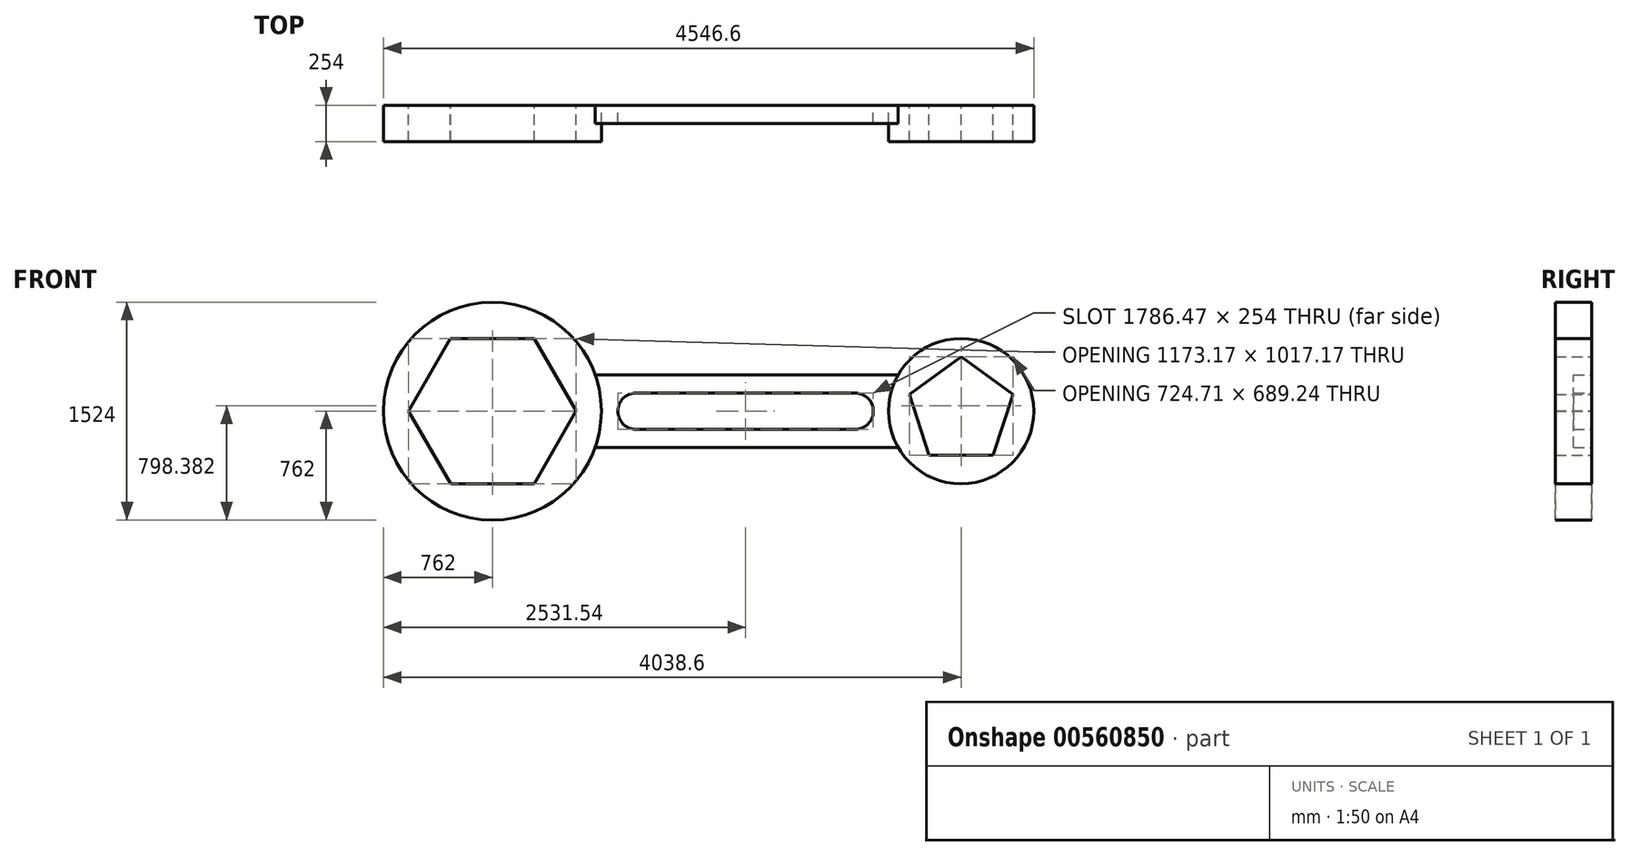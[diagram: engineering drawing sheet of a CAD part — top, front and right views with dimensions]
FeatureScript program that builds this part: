
annotation { "Feature Type Name" : "Feature", "Feature Type Description" : "" }
export const myFeature = defineFeature(function(context is Context, id is Id, definition is map)
    precondition{}
    {
        {
            var Q0;
            Q0=qCreatedBy(makeId("Front.planeOp"),FACE);
            var sketch = newSketch(context, id + "F0", { "sketchPlane" : qUnion([Q0])});
            skCircle(sketch, "E0", {"center": v(0, 0) * mm, "radius": 762 * mm});
            skLineSegment(sketch, "E1", {"start": v(762, 0) * mm, "end": v(2768.6, 0) * mm});
            skCircle(sketch, "E2", {"center": v(3276.6, 0) * mm, "radius": 508 * mm});
            skLineSegment(sketch, "E3", {"start": v(1765.3, 0) * mm, "end": v(1765.3, 127) * mm});
            skLineSegment(sketch, "E4", {"start": v(1765.3, 127) * mm, "end": v(1003.3, 127) * mm});
            skLineSegment(sketch, "E5", {"start": v(1003.3, -127) * mm, "end": v(2535.77, -127) * mm});
            skLineSegment(sketch, "E6", {"start": v(2535.77, 127) * mm, "end": v(1765.3, 127) * mm});
            skLineSegment(sketch, "E7", {"start": v(1765.3, 0) * mm, "end": v(1765.3, 254) * mm});
            skPoint(sketch, "E7.endSnap0", {"position": v(1765.3, 63.5) * mm});
            skLineSegment(sketch, "E8", {"start": v(1765.3, 254) * mm, "end": v(718.42, 254) * mm});
            skLineSegment(sketch, "E9", {"start": v(1765.3, 254) * mm, "end": v(2836.66, 254) * mm});
            skLineSegment(sketch, "E10.MirrorCS", {"start": v(750.33, 0) * mm, "end": v(2756.93, 0) * mm});
            skLineSegment(sketch, "E11.MirrorCS", {"start": v(1765.3, -254) * mm, "end": v(2836.66, -254) * mm});
            skLineSegment(sketch, "E12.MirrorCS", {"start": v(1765.3, -254) * mm, "end": v(718.42, -254) * mm});
            skCircle(sketch, "E13.cCircle", {"center": v(0, 0) * mm, "radius": 508 * mm, "construction": true});
            skLineSegment(sketch, "E13.0", {"start": v(292.28, 508.58) * mm, "end": v(586.59, 1.17) * mm});
            skLineSegment(sketch, "E13.1", {"start": v(586.59, 1.17) * mm, "end": v(294.3, -507.41) * mm});
            skLineSegment(sketch, "E13.2", {"start": v(294.3, -507.41) * mm, "end": v(-292.28, -508.58) * mm});
            skLineSegment(sketch, "E13.3", {"start": v(-292.28, -508.58) * mm, "end": v(-586.59, -1.17) * mm});
            skLineSegment(sketch, "E13.4", {"start": v(-586.59, -1.17) * mm, "end": v(-294.3, 507.41) * mm});
            skLineSegment(sketch, "E13.5", {"start": v(-294.3, 507.41) * mm, "end": v(292.28, 508.58) * mm});
            skPoint(sketch, "E13.0.midPoint", {"position": v(439.43, 254.88) * mm});
            skCircle(sketch, "E14.cCircle", {"center": v(3276.6, 0) * mm, "radius": 308.24 * mm, "construction": true});
            skLineSegment(sketch, "E14.0", {"start": v(2914.25, 117.73) * mm, "end": v(3276.6, 381) * mm});
            skLineSegment(sketch, "E14.1", {"start": v(3276.6, 381) * mm, "end": v(3638.95, 117.74) * mm});
            skLineSegment(sketch, "E14.2", {"start": v(3638.95, 117.74) * mm, "end": v(3500.55, -308.23) * mm});
            skLineSegment(sketch, "E14.3", {"start": v(3500.55, -308.23) * mm, "end": v(3052.66, -308.24) * mm});
            skLineSegment(sketch, "E14.4", {"start": v(3052.66, -308.24) * mm, "end": v(2914.25, 117.73) * mm});
            skPoint(sketch, "E14.0.midPoint", {"position": v(3095.42, 249.37) * mm});
            skLineSegment(sketch, "E15", {"start": v(3276.6, 381) * mm, "end": v(3276.6, 0) * mm});
            skLineSegment(sketch, "E16", {"start": v(0, 508) * mm, "end": v(0, 0) * mm});
            skPoint(sketch, "E17.visualSharp", {"position": v(876.3, 127) * mm});
            skArc(sketch, "E18", {"start": v(1003.3, 127) * mm, "mid": v(876.3, 0) * mm, "end": v(1003.3, -127) * mm});
            skPoint(sketch, "E19.orphan", {"position": v(876.3, -127) * mm});
            skArc(sketch, "E20", {"start": v(2535.77, -127) * mm, "mid": v(2662.77, 0) * mm, "end": v(2535.77, 127) * mm});
            skSolve(sketch);
        }
        {
            var Q0;
            {var subQ5=sQuery(id+"F0.wireOp",EDGE,"E13.0");Q0=makeQuery(id+"F0.imprint","IMPRINT",FACE,{"disambiguationData":[TD([[makeQuery(id+"F0.imprint","IMPRINT",EDGE,{"derivedFrom":subQ5}),1.0]])]});}
            var Q1;
            Q1=makeQuery(id+"F0.imprint","IMPRINT",FACE,{"disambiguationData":[TD([[makeQuery(id+"F0.imprint","IMPRINT",EDGE,{"derivedFrom":sQuery(id+"F0.wireOp",EDGE,"E14.0")}),1.0]])]});
            extrude(context, id + "F1", {"entities" : qUnion([Q0, Q1]), "depth" : 254 * mm, "offsetDistance" : 25.4 * mm});
        }
        {
            var Q0;
            {var subQ4=sQuery(id+"F0.wireOp",EDGE,"E1");Q0=makeQuery(id+"F0.imprint","IMPRINT",FACE,{"disambiguationData":[TD([[makeQuery(id+"F0.imprint","IMPRINT",EDGE,{"derivedFrom":subQ4}),1.0]])]});}
            var Q1;
            {var subQ1=sQuery(id+"F0.wireOp",EDGE,"E4");Q1=makeQuery(id+"F0.imprint","IMPRINT",FACE,{"disambiguationData":[TD([[makeQuery(id+"F0.imprint","IMPRINT",EDGE,{"derivedFrom":subQ1}),-1.0]])]});}
            var Q2;
            {var subQ1=sQuery(id+"F0.wireOp",EDGE,"E1");Q2=makeQuery(id+"F0.imprint","IMPRINT",FACE,{"disambiguationData":[TD([[makeQuery(id+"F0.imprint","IMPRINT",EDGE,{"derivedFrom":subQ1}),-1.0]])]});}
            extrude(context, id + "F2", {"entities" : qUnion([Q0, Q1, Q2]), "depth" : 127 * mm, "offsetDistance" : 25.4 * mm});
        }
    });
